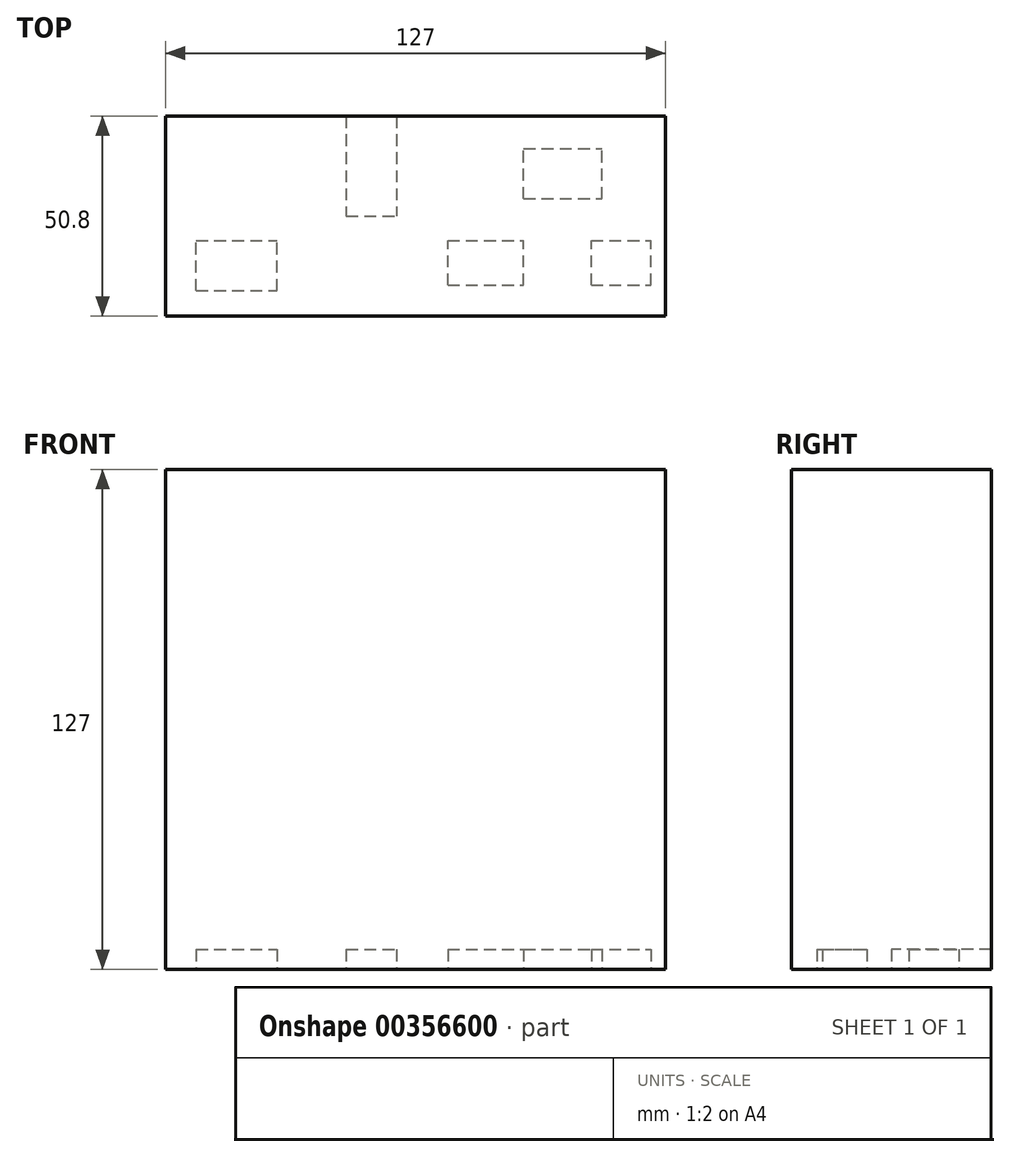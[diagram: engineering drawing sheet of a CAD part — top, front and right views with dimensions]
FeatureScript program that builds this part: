
annotation { "Feature Type Name" : "Feature", "Feature Type Description" : "" }
export const myFeature = defineFeature(function(context is Context, id is Id, definition is map)
    precondition{}
    {
        {
            var Q0;
            Q0=qCreatedBy(makeId("Front.planeOp"),FACE);
            var sketch = newSketch(context, id + "F0", { "sketchPlane" : qUnion([Q0])});
            skLineSegment(sketch, "E0.bottom", {"start": v(-74.45, 73.3) * mm, "end": v(52.55, 73.3) * mm});
            skLineSegment(sketch, "E0.top", {"start": v(-74.45, -53.7) * mm, "end": v(52.55, -53.7) * mm});
            skLineSegment(sketch, "E0.left", {"start": v(-74.45, 73.3) * mm, "end": v(-74.45, -53.7) * mm});
            skLineSegment(sketch, "E0.right", {"start": v(52.55, 73.3) * mm, "end": v(52.55, -53.7) * mm});
            skSolve(sketch);
        }
        {
            var Q0;
            Q0=makeQuery(id+"F0.imprint","IMPRINT",FACE,{"disambiguationData":[TD([[makeQuery(id+"F0.imprint","IMPRINT",EDGE,{"derivedFrom":sQuery(id+"F0.wireOp",EDGE,"E0.bottom")}),-1.0]])]});
            extrude(context, id + "F1", {"entities" : qUnion([Q0]), "depth" : 50.8 * mm});
        }
        {
            var Q0;
            Q0=makeQuery(id+"F1.opExtrude","SWEPT_FACE",FACE,{"disambiguationData":[OSD([sQuery(id+"F0.wireOp",EDGE,"E0.top")])]});
            var sketch = newSketch(context, id + "F2", { "sketchPlane" : qUnion([Q0])});
            skLineSegment(sketch, "E1.bottom", {"start": v(-28.54, 0) * mm, "end": v(-15.84, 0) * mm});
            skLineSegment(sketch, "E1.top", {"start": v(-28.54, 25.4) * mm, "end": v(-15.84, 25.4) * mm});
            skLineSegment(sketch, "E1.left", {"start": v(-28.54, 0) * mm, "end": v(-28.54, 25.4) * mm});
            skLineSegment(sketch, "E1.right", {"start": v(-15.84, 0) * mm, "end": v(-15.84, 25.4) * mm});
            skLineSegment(sketch, "E2.bottom", {"start": v(-66.71, 44.36) * mm, "end": v(-46.08, 44.36) * mm});
            skLineSegment(sketch, "E2.top", {"start": v(-66.71, 31.64) * mm, "end": v(-46.08, 31.64) * mm});
            skLineSegment(sketch, "E2.left", {"start": v(-66.71, 44.36) * mm, "end": v(-66.71, 31.64) * mm});
            skLineSegment(sketch, "E2.right", {"start": v(-46.08, 44.36) * mm, "end": v(-46.08, 31.64) * mm});
            skLineSegment(sketch, "E3.bottom", {"start": v(-2.75, 42.98) * mm, "end": v(16.5, 42.98) * mm});
            skLineSegment(sketch, "E3.top", {"start": v(-2.75, 31.64) * mm, "end": v(16.5, 31.64) * mm});
            skLineSegment(sketch, "E3.left", {"start": v(-2.75, 42.98) * mm, "end": v(-2.75, 31.64) * mm});
            skLineSegment(sketch, "E3.right", {"start": v(16.5, 42.98) * mm, "end": v(16.5, 31.64) * mm});
            skLineSegment(sketch, "E4.bottom", {"start": v(16.5, 20.98) * mm, "end": v(36.45, 20.98) * mm});
            skLineSegment(sketch, "E4.top", {"start": v(16.5, 8.25) * mm, "end": v(36.45, 8.25) * mm});
            skLineSegment(sketch, "E4.left", {"start": v(16.5, 20.98) * mm, "end": v(16.5, 8.25) * mm});
            skLineSegment(sketch, "E4.right", {"start": v(36.45, 20.98) * mm, "end": v(36.45, 8.25) * mm});
            skPoint(sketch, "E5.firstSnap0", {"position": v(6.88, 42.98) * mm});
            skLineSegment(sketch, "E5.bottom", {"start": v(33.7, 42.98) * mm, "end": v(48.83, 42.98) * mm});
            skLineSegment(sketch, "E5.top", {"start": v(33.7, 31.64) * mm, "end": v(48.83, 31.64) * mm});
            skLineSegment(sketch, "E5.left", {"start": v(33.7, 42.98) * mm, "end": v(33.7, 31.64) * mm});
            skLineSegment(sketch, "E5.right", {"start": v(48.83, 42.98) * mm, "end": v(48.83, 31.64) * mm});
            skSolve(sketch);
        }
        {
            var Q0;
            Q0=makeQuery(id+"F2.imprint","IMPRINT",FACE,{"disambiguationData":[TD([[makeQuery(id+"F2.imprint","IMPRINT",EDGE,{"derivedFrom":sQuery(id+"F2.wireOp",EDGE,"E2.bottom")}),-1.0]])]});
            var Q1;
            Q1=makeQuery(id+"F2.imprint","IMPRINT",FACE,{"disambiguationData":[TD([[makeQuery(id+"F2.imprint","IMPRINT",EDGE,{"derivedFrom":sQuery(id+"F2.wireOp",EDGE,"E1.bottom")}),1.0]])]});
            var Q2;
            Q2=makeQuery(id+"F2.imprint","IMPRINT",FACE,{"disambiguationData":[TD([[makeQuery(id+"F2.imprint","IMPRINT",EDGE,{"derivedFrom":sQuery(id+"F2.wireOp",EDGE,"E3.bottom")}),-1.0]])]});
            var Q3;
            Q3=makeQuery(id+"F2.imprint","IMPRINT",FACE,{"disambiguationData":[TD([[makeQuery(id+"F2.imprint","IMPRINT",EDGE,{"derivedFrom":sQuery(id+"F2.wireOp",EDGE,"E5.bottom")}),-1.0]])]});
            var Q4;
            Q4=makeQuery(id+"F2.imprint","IMPRINT",FACE,{"disambiguationData":[TD([[makeQuery(id+"F2.imprint","IMPRINT",EDGE,{"derivedFrom":sQuery(id+"F2.wireOp",EDGE,"E4.bottom")}),-1.0]])]});
            extrude(context, id + "F3", {"entities" : qUnion([Q0, Q1, Q2, Q3, Q4]), "operationType" : NewBodyOperationType.REMOVE, "oppositeDirection" : true, "depth" : 5.08 * mm});
        }
    });
